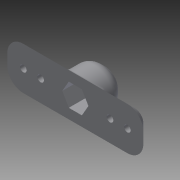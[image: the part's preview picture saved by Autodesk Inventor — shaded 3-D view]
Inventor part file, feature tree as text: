
AUTODESK INVENTOR PART (.ipt)
format: ipt  version: 2014 SP2 (Build 180246200, 246)  size: 414,208 bytes
history: native  units: mm
features: sketch x6, extrude x4, chamfer x3, fillet x3
ambient origin geometry x8: Origin, YZ Plane, XZ Plane, XY Plane, X Axis, Y Axis, Z Axis, Center Point
bodies: Solid1 (feature_tree)
feature tree (16):
  extrude  "Extrusion1"  Depth=2.5mm
  chamfer  "Chamfer1"  Distance=6.5mm
  extrude  "Extrusion2"  Depth=13.0mm
  extrude  "Extrusion3"  Depth=16.0mm
  chamfer  "Chamfer2"  Distance=8.0mm
  sketch  "Sketch4"  dims[d4=13.0mm]
  extrude  "Extrusion4"  Depth=6.0mm
  chamfer  "Chamfer3"  Distance=6.0mm
  sketch  "Sketch6"  dims[d6=2.5mm d7=6.5mm d8=13.0mm d9=16.0mm d10=8.0mm d11=6.0mm d12=6.0mm d13=6.0mm d14=8.0mm d15=14.0mm d16=5.5mm d17=3.0mm d18=0.0mm d19=3.0mm d20=2.0mm d21=45.0deg d22=10.0mm d23=8.0mm d24=0.0mm d25=8.5mm d26=7.0mm d27=0.0mm d28=4.0mm d29=2.0mm d30=45.0deg d31=15.0mm d32=11.0mm d33=0.0mm d34=2.5mm d35=2.0mm d36=45.0deg d37=4.0mm d38=2.0mm d39=1.0mm]
  fillet  "Fillet1"  Radius=6.0mm
  fillet  "Fillet2"  Radius=8.0mm
  fillet  "Fillet3"  Radius=14.0mm
  sketch  "Sketch1"  dims[d0=2.5mm d1=2.5mm]
  sketch  "Sketch2"  dims[d2=6.5mm]
  sketch  "Sketch3"  dims[d3=110.0mm]
  sketch  "Sketch5"  dims[d5=2.5mm]
